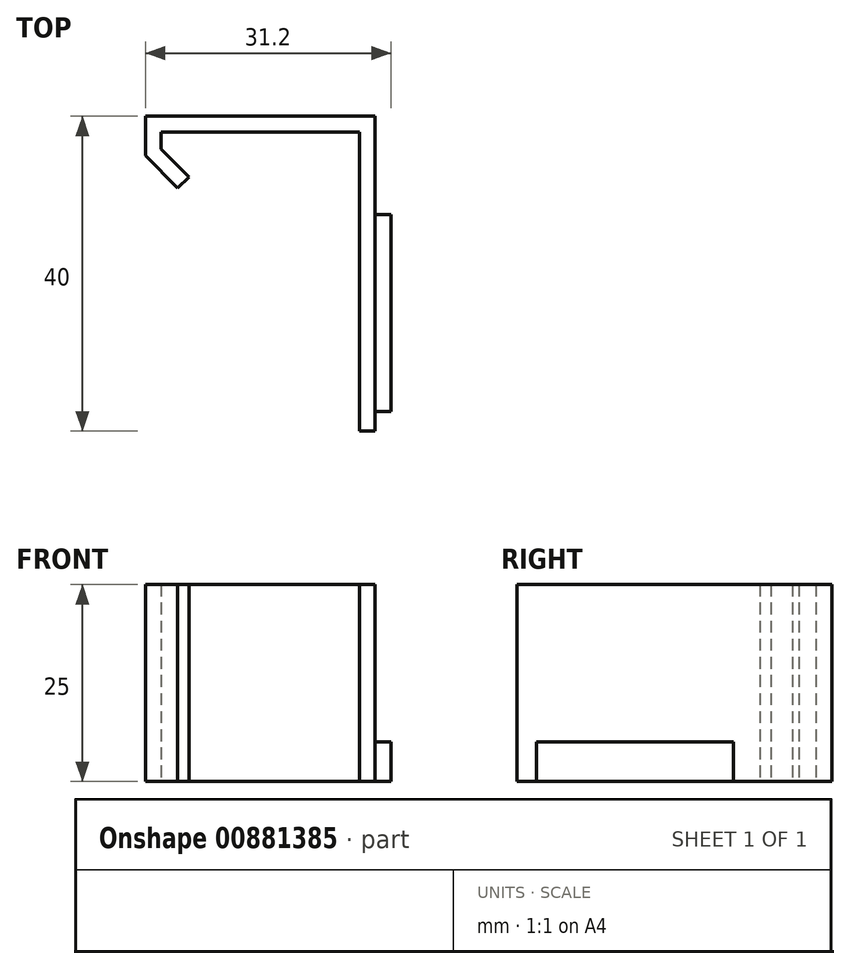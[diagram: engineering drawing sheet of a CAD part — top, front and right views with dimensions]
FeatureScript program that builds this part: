
annotation { "Feature Type Name" : "Feature", "Feature Type Description" : "" }
export const myFeature = defineFeature(function(context is Context, id is Id, definition is map)
    precondition{}
    {
        {
            var Q0;
            Q0=qCreatedBy(makeId("Top.planeOp"),FACE);
            var sketch = newSketch(context, id + "F0", { "sketchPlane" : qUnion([Q0])});
            skLineSegment(sketch, "E0", {"start": v(0, 0) * mm, "end": v(2, 0) * mm});
            skLineSegment(sketch, "E1", {"start": v(2, 0) * mm, "end": v(2, 25) * mm});
            skLineSegment(sketch, "E2", {"start": v(2, 25) * mm, "end": v(-23, 25) * mm});
            skLineSegment(sketch, "E3", {"start": v(-23, 25) * mm, "end": v(-23, 23) * mm});
            skLineSegment(sketch, "E4", {"start": v(-23, 23) * mm, "end": v(0, 23) * mm});
            skLineSegment(sketch, "E5", {"start": v(0, 23) * mm, "end": v(0, 0) * mm});
            skLineSegment(sketch, "E6", {"start": v(-23.1, 22.9) * mm, "end": v(-23.1, 25.1) * mm});
            skLineSegment(sketch, "E7", {"start": v(-23.1, 25.1) * mm, "end": v(2.1, 25.1) * mm});
            skLineSegment(sketch, "E8", {"start": v(2.1, 25.1) * mm, "end": v(2.1, -12.9) * mm});
            skLineSegment(sketch, "E9", {"start": v(-23.1, 22.9) * mm, "end": v(-19.56, 19.36) * mm});
            skLineSegment(sketch, "E10", {"start": v(2.1, 25.1) * mm, "end": v(13.17, 14.03) * mm, "construction": true});
            skLineSegment(sketch, "E11", {"start": v(-19.56, 19.36) * mm, "end": v(7.84, 19.36) * mm, "construction": true});
            skPoint(sketch, "E12", {"position": v(2.1, 19.36) * mm});
            skLineSegment(sketch, "E13", {"start": v(-19.56, 19.36) * mm, "end": v(-20.98, 17.95) * mm});
            skLineSegment(sketch, "E14", {"start": v(-20.98, 17.95) * mm, "end": v(-25.1, 22.07) * mm});
            skLineSegment(sketch, "E15", {"start": v(-25.1, 22.07) * mm, "end": v(-25.1, 27.1) * mm});
            skLineSegment(sketch, "E16", {"start": v(-25.1, 27.1) * mm, "end": v(4.1, 27.1) * mm});
            skLineSegment(sketch, "E17", {"start": v(4.1, 27.1) * mm, "end": v(4.1, -12.9) * mm});
            skLineSegment(sketch, "E18", {"start": v(4.1, -12.9) * mm, "end": v(2.1, -12.9) * mm});
            skLineSegment(sketch, "E19", {"start": v(-23.1, 22.9) * mm, "end": v(-24.51, 21.49) * mm, "construction": true});
            skLineSegment(sketch, "E20.bottom", {"start": v(4.1, -10.4) * mm, "end": v(6.1, -10.4) * mm});
            skLineSegment(sketch, "E20.top", {"start": v(4.1, 14.6) * mm, "end": v(6.1, 14.6) * mm});
            skLineSegment(sketch, "E20.left", {"start": v(4.1, -10.4) * mm, "end": v(4.1, 14.6) * mm});
            skLineSegment(sketch, "E20.right", {"start": v(6.1, -10.4) * mm, "end": v(6.1, 14.6) * mm});
            skSolve(sketch);
        }
        {
            var Q0;
            Q0=makeQuery(id+"F0.imprint","IMPRINT",FACE,{"disambiguationData":[TD([[makeQuery(id+"F0.imprint","IMPRINT",EDGE,{"derivedFrom":sQuery(id+"F0.wireOp",EDGE,"E6")}),1.0]])]});
            extrude(context, id + "F1", {"entities" : qUnion([Q0]), "depth" : 25 * mm, "offsetDistance" : 25 * mm});
        }
        {
            var Q0;
            Q0=makeQuery(id+"F0.imprint","IMPRINT",FACE,{"disambiguationData":[TD([[makeQuery(id+"F0.imprint","IMPRINT",EDGE,{"derivedFrom":sQuery(id+"F0.wireOp",EDGE,"E20.bottom")}),1.0]])]});
            extrude(context, id + "F2", {"entities" : qUnion([Q0]), "operationType" : NewBodyOperationType.ADD, "depth" : 5 * mm, "offsetDistance" : 25 * mm});
        }
    });
